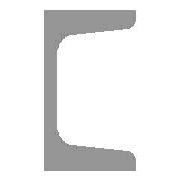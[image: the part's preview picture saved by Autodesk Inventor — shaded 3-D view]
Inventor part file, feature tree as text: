
AUTODESK INVENTOR PART (.ipt)
format: ipt  version: 2025 (Build 290162010, 162A)  size: 154,112 bytes
history: native  units: mm (DEFAULTED — no unit token found)
features: other x3, sketch x2, extrude x1, plane x1
ambient origin geometry x8: Origin, YZ Plane, XZ Plane, XY Plane, X Axis, Y Axis, Z Axis, Center Point
bodies: Solid1 (feature_tree), Body (feature_tree)
feature tree (7):
  other  "Driven Length"
  other  "Start plane"
  other  "End plane"
  extrude  "Extrusion2"  Depth=60.0mm
  sketch  "Sketch3"  dims[d0=6.3mm d1=60.0mm]
  plane  "Work Plane3"
  sketch  "Sketch5"  dims[d2=55.0mm d3=8.5mm d4=24.35mm d5=2.559282mm d6=140.0mm d7=0.0mm d23=8.0mm d24=4.5mm d25=1.6mm d26=-0.0mm d27=140.0mm d28=90.0deg d29=140.0mm d30=17.0mm d31=20.0mm d32=70.0mm d33=0.0mm d34=0.0mm]
